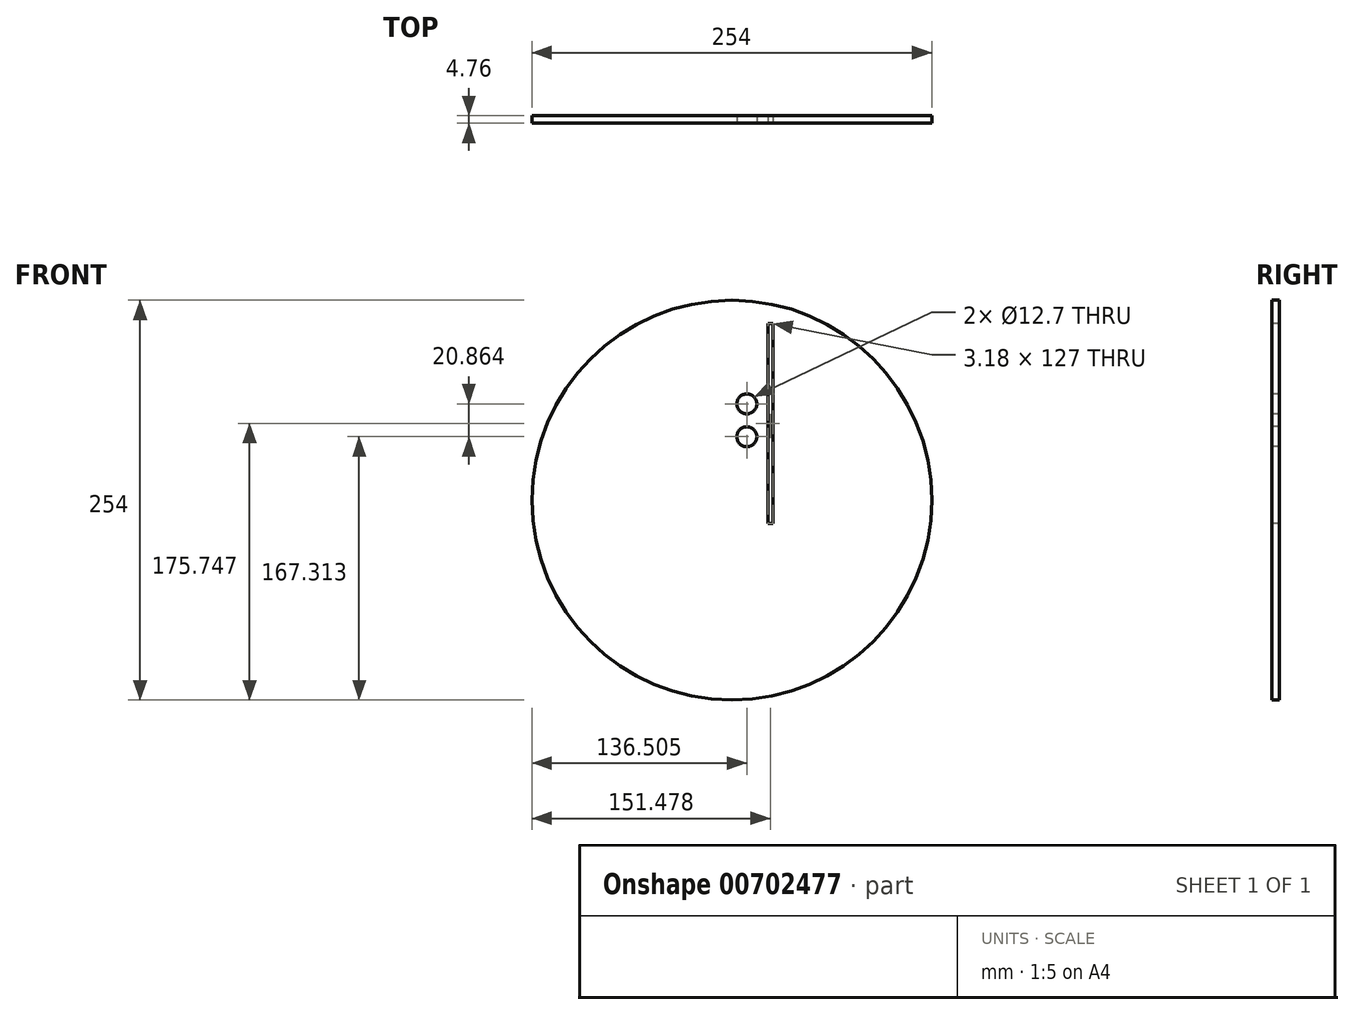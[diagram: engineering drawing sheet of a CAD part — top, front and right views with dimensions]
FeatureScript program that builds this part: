
annotation { "Feature Type Name" : "Feature", "Feature Type Description" : "" }
export const myFeature = defineFeature(function(context is Context, id is Id, definition is map)
    precondition{}
    {
        {
            var Q0;
            Q0=qCreatedBy(makeId("Front.planeOp"),FACE);
            var sketch = newSketch(context, id + "F0", { "sketchPlane" : qUnion([Q0])});
            skCircle(sketch, "E0", {"center": v(0, 0) * mm, "radius": 127 * mm});
            skSolve(sketch);
        }
        {
            var Q0;
            Q0=makeQuery(id+"F0.imprint","IMPRINT",FACE,{"disambiguationData":[TD([[makeQuery(id+"F0.imprint","IMPRINT",EDGE,{"derivedFrom":sQuery(id+"F0.wireOp",EDGE,"E0")}),1.0]])]});
            extrude(context, id + "F1", {"entities" : qUnion([Q0]), "depth" : 4.76 * mm, "offsetDistance" : 25.4 * mm});
        }
        {
            var Q0;
            Q0=makeQuery(id+"F1.opExtrude","CAP_FACE",FACE,{"disambiguationData":[OSD([sQuery(id+"F0.wireOp",EDGE,"E0")])],"isStart":false});
            var sketch = newSketch(context, id + "F2", { "sketchPlane" : qUnion([Q0])});
            skLineSegment(sketch, "E1.bottom", {"start": v(-228.07, 4.12) * mm, "end": v(-215.37, 4.12) * mm});
            skLineSegment(sketch, "E1.top", {"start": v(-228.07, -72.08) * mm, "end": v(-215.37, -72.08) * mm});
            skLineSegment(sketch, "E1.left", {"start": v(-228.07, 4.12) * mm, "end": v(-228.07, -72.08) * mm});
            skLineSegment(sketch, "E1.right", {"start": v(-215.37, 4.12) * mm, "end": v(-215.37, -72.08) * mm});
            skSolve(sketch);
        }
        {
            var Q0;
            Q0=makeQuery(id+"F2.imprint","IMPRINT",FACE,{"disambiguationData":[TD([[makeQuery(id+"F2.imprint","IMPRINT",EDGE,{"derivedFrom":sQuery(id+"F2.wireOp",EDGE,"E1.bottom")}),-1.0]])]});
            extrude(context, id + "F3", {"entities" : qUnion([Q0]), "depth" : 25.4 * mm, "offsetDistance" : 25.4 * mm});
        }
        {
            var Q0;
            Q0=makeQuery(id+"F3.opExtrude","CAP_EDGE",EDGE,{"disambiguationData":[OSD([sQuery(id+"F2.wireOp",EDGE,"E1.left")])],"isStart":false});
            var Q1;
            Q1=makeQuery(id+"F3.opExtrude","CAP_EDGE",EDGE,{"disambiguationData":[OSD([sQuery(id+"F2.wireOp",EDGE,"E1.right")])],"isStart":false});
            var Q2;
            Q2=makeQuery(id+"F3.opExtrude","CAP_EDGE",EDGE,{"disambiguationData":[OSD([sQuery(id+"F2.wireOp",EDGE,"E1.bottom")])],"isStart":false});
            var Q3;
            Q3=makeQuery(id+"F3.opExtrude","CAP_EDGE",EDGE,{"disambiguationData":[OSD([sQuery(id+"F2.wireOp",EDGE,"E1.top")])],"isStart":false});
            chamfer(context, id + "F4", {"entities" : qUnion([Q0, Q1, Q2, Q3]), "width" : 5.08 * mm, "tangentPropagation" : true});
        }
        {
            var Q0;
            Q0=makeQuery(id+"F1.opExtrude","CAP_FACE",FACE,{"disambiguationData":[OSD([sQuery(id+"F0.wireOp",EDGE,"E0")])],"isStart":false});
            var sketch = newSketch(context, id + "F5", { "sketchPlane" : qUnion([Q0])});
            skCircle(sketch, "E2", {"center": v(9.5, 61.18) * mm, "radius": 6.35 * mm});
            skCircle(sketch, "E3", {"center": v(9.5, 40.31) * mm, "radius": 6.35 * mm});
            skSolve(sketch);
        }
        {
            var Q0;
            Q0=makeQuery(id+"F5.imprint","IMPRINT",FACE,{"disambiguationData":[TD([[makeQuery(id+"F5.imprint","IMPRINT",EDGE,{"derivedFrom":sQuery(id+"F5.wireOp",EDGE,"E2")}),1.0]])]});
            var Q1;
            Q1=makeQuery(id+"F5.imprint","IMPRINT",FACE,{"disambiguationData":[TD([[makeQuery(id+"F5.imprint","IMPRINT",EDGE,{"derivedFrom":sQuery(id+"F5.wireOp",EDGE,"E3")}),1.0]])]});
            extrude(context, id + "F6", {"entities" : qUnion([Q0, Q1]), "operationType" : NewBodyOperationType.REMOVE, "endBound" : BoundingType.THROUGH_ALL, "oppositeDirection" : true, "depth" : 25.4 * mm, "offsetDistance" : 25.4 * mm});
        }
        {
            var Q0;
            Q0=makeQuery(id+"F2.imprint","IMPRINT",FACE,{"disambiguationData":[TD([[makeQuery(id+"F2.imprint","IMPRINT",EDGE,{"derivedFrom":makeQuery(id+"F1.opExtrude","CAP_EDGE",EDGE,{"disambiguationData":[OSD([sQuery(id+"F0.wireOp",EDGE,"E0")])],"isStart":false})}),1.0]])]});
            var sketch = newSketch(context, id + "F7", { "sketchPlane" : qUnion([Q0])});
            skLineSegment(sketch, "E4.bottom", {"start": v(22.9, 112.25) * mm, "end": v(26.07, 112.25) * mm});
            skLineSegment(sketch, "E4.top", {"start": v(22.9, -14.75) * mm, "end": v(26.07, -14.75) * mm});
            skLineSegment(sketch, "E4.left", {"start": v(22.9, 112.25) * mm, "end": v(22.9, -14.75) * mm});
            skLineSegment(sketch, "E4.right", {"start": v(26.07, 112.25) * mm, "end": v(26.07, -14.75) * mm});
            skSolve(sketch);
        }
        {
            var Q0;
            Q0=makeQuery(id+"F7.imprint","IMPRINT",FACE,{"disambiguationData":[TD([[makeQuery(id+"F7.imprint","IMPRINT",EDGE,{"derivedFrom":sQuery(id+"F7.wireOp",EDGE,"E4.bottom")}),-1.0]])]});
            extrude(context, id + "F8", {"entities" : qUnion([Q0]), "operationType" : NewBodyOperationType.REMOVE, "endBound" : BoundingType.THROUGH_ALL, "oppositeDirection" : true, "depth" : 25.4 * mm, "offsetDistance" : 25.4 * mm});
        }
        {
            var Q0;
            Q0=makeQuery(id+"F3.opExtrude","SWEPT_BODY",BODY,{"disambiguationData":[OSD([sQuery(id+"F2.wireOp",EDGE,"E1.bottom"),sQuery(id+"F2.wireOp",EDGE,"E1.top"),sQuery(id+"F2.wireOp",EDGE,"E1.left"),sQuery(id+"F2.wireOp",EDGE,"E1.right")])]});
            deleteBodies(context, id + "F9", {"entities" : qUnion([Q0])});
        }
    });
